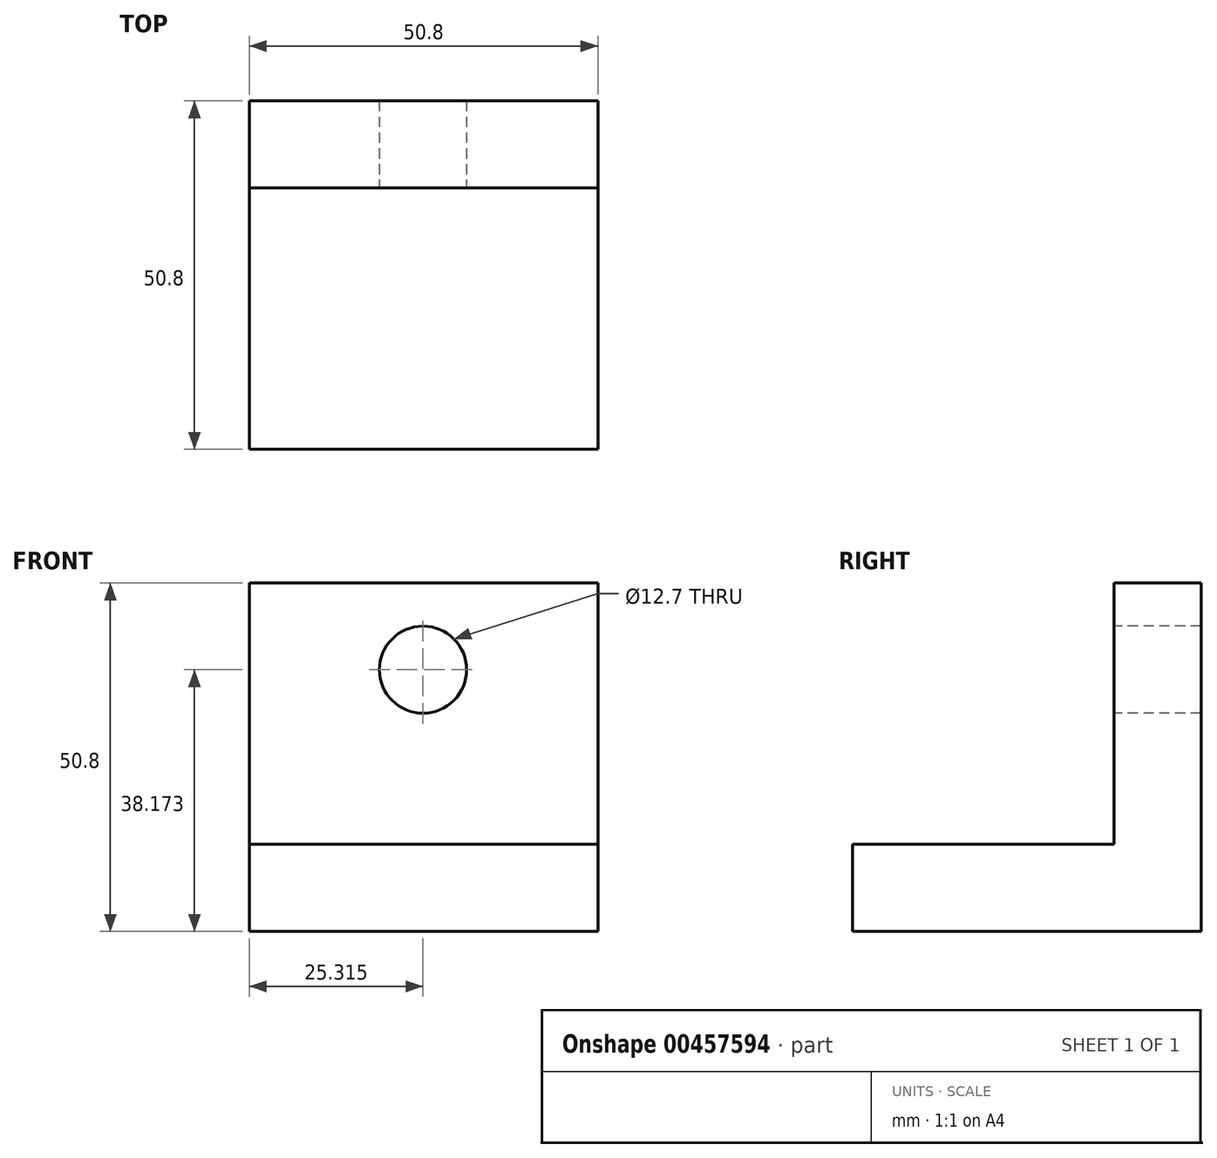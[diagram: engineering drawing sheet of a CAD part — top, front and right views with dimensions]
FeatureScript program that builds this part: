
annotation { "Feature Type Name" : "Feature", "Feature Type Description" : "" }
export const myFeature = defineFeature(function(context is Context, id is Id, definition is map)
    precondition{}
    {
        {
            var Q0;
            Q0=qCreatedBy(makeId("Top.planeOp"),FACE);
            var sketch = newSketch(context, id + "F0", { "sketchPlane" : qUnion([Q0])});
            skLineSegment(sketch, "E0.bottom", {"start": v(-48.07, 63.15) * mm, "end": v(2.73, 63.15) * mm});
            skLineSegment(sketch, "E0.top", {"start": v(-48.07, 12.35) * mm, "end": v(2.73, 12.35) * mm});
            skLineSegment(sketch, "E0.left", {"start": v(-48.07, 63.15) * mm, "end": v(-48.07, 12.35) * mm});
            skLineSegment(sketch, "E0.right", {"start": v(2.73, 63.15) * mm, "end": v(2.73, 12.35) * mm});
            skLineSegment(sketch, "E1", {"start": v(-48.07, 50.45) * mm, "end": v(2.73, 50.45) * mm});
            skSolve(sketch);
        }
        {
            var Q0;
            {var subQ0=sQuery(id+"F0.wireOp",EDGE,"E0.top");Q0=makeQuery(id+"F0.imprint","IMPRINT",FACE,{"disambiguationData":[TD([[makeQuery(id+"F0.imprint","IMPRINT",EDGE,{"derivedFrom":subQ0}),1.0]])]});}
            extrude(context, id + "F1", {"entities" : qUnion([Q0]), "depth" : 12.7 * mm});
        }
        {
            var Q0;
            {var subQ0=sQuery(id+"F0.wireOp",EDGE,"E0.bottom");Q0=makeQuery(id+"F0.imprint","IMPRINT",FACE,{"disambiguationData":[TD([[makeQuery(id+"F0.imprint","IMPRINT",EDGE,{"derivedFrom":subQ0}),-1.0]])]});}
            extrude(context, id + "F2", {"entities" : qUnion([Q0]), "operationType" : NewBodyOperationType.ADD, "depth" : 50.8 * mm});
        }
        {
            var Q0;
            Q0=makeQuery(id+"F2.opExtrude","SWEPT_FACE",FACE,{"disambiguationData":[OSD([sQuery(id+"F0.wireOp",EDGE,"E1")])]});
            var sketch = newSketch(context, id + "F3", { "sketchPlane" : qUnion([Q0])});
            skCircle(sketch, "E2", {"center": v(-22.76, 38.17) * mm, "radius": 6.35 * mm});
            skSolve(sketch);
        }
        {
            var Q0;
            Q0=sQuery(id+"F3.wireOp",VERTEX,"E2.center");
            var Q1;
            Q1=makeQuery(id+"F1.opExtrude","SWEPT_BODY",BODY,{"disambiguationData":[OSD([sQuery(id+"F0.wireOp",EDGE,"E0.top"),sQuery(id+"F0.wireOp",EDGE,"E0.left"),sQuery(id+"F0.wireOp",EDGE,"E0.right"),sQuery(id+"F0.wireOp",EDGE,"E1")])]});
            hole(context, id + "F4", {"style" : HoleStyle.SIMPLE, "endStyle" : HoleEndStyle.THROUGH, "holeDiameter" : 12.7 * mm, "isTappedThrough" : true, "tappedDepth" : 12.7 * mm, "tapClearance" : 3, "locations" : qUnion([Q0]), "scope" : qUnion([Q1])});
        }
    });
